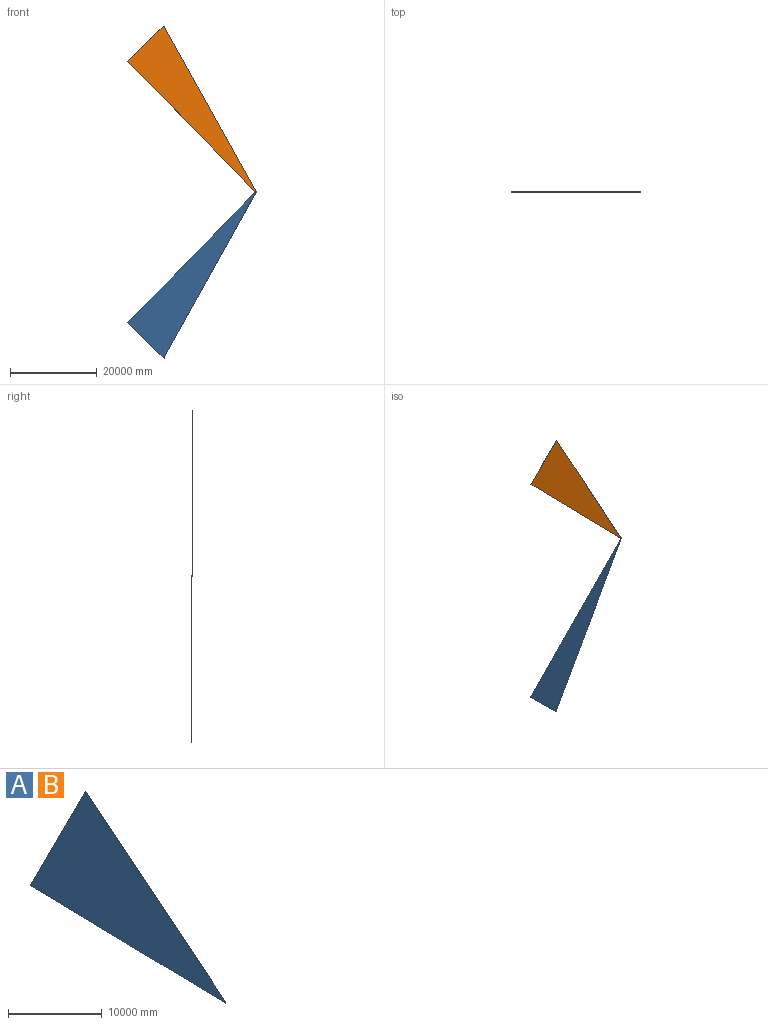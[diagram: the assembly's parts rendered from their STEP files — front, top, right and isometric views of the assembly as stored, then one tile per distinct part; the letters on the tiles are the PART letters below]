
ASSEMBLY  parts=2 mates=1
PART A: 16 faces, bbox 29537x197.9x38271.4 mm
  f0: plane 12.51x11.03mm, normal (0,-1,0), area 34.1mm2, adj f1,f7,f15
  f1: plane 87.66x10.3mm, normal (-0.97,0,-0.24), area 931.1mm2, adj f0,f2,f7,f8,f9,f13,f15
  f2: plane 87.66x8.75mm, normal (-0.75,0,0.67), area 1027.2mm2, adj f1,f3,f8,f9
  f3: plane 87.66x63.01mm, normal (-0.64,0,-0.77), area 7198.1mm2, adj f2,f4,f8,f9
  f4: plane 87.66x83.8mm, normal (0.7,0,-0.72), area 10239.7mm2, adj f3,f5,f8,f9,f11
  f5: plane 87.66x79.55mm, normal (0.87,0,0.49), area 7975.6mm2, adj f4,f6,f9,f10
  f6: plane 87.66x84.93mm, normal (-0.7,0,0.71), area 10412.2mm2, adj f5,f7,f9,f15
  f7: plane 87.66x12.51mm, normal (-0.44,0,0.9), area 1223mm2, adj f0,f1,f6,f9
  f8: plane 65.64x61.8mm, normal (0,-1,0), area 640.3mm2, adj f1,f2,f3,f4,f13
  f9: plane 160.94x146.81mm, normal (0,1,0), area 11632mm2, adj f1,f2,f3,f4,f5,f6,f7
  f10: plane 38190.04x21206.94mm, normal (0.87,0,0.49), area 1608841.7mm2, adj f5,f11,f12,f14,f15
  f11: plane 81.22x78.89mm, normal (0.7,0,-0.72), area 4150.4mm2, adj f4,f10,f13,f14
  f12: plane 8330.07x8145.44mm, normal (-0.7,0,0.71), area 429092.1mm2, adj f10,f13,f14,f15
  f13: plane 30123.49x29455.8mm, normal (-0.71,0,-0.7), area 1551698.8mm2, adj f1,f8,f11,f12,f14,f15
  f14: plane 38268.83x29536.93mm, normal (0,-1,0), area 247815295.6mm2, adj f10,f11,f12,f13
  f15: plane 38209.58x29492.76mm, normal (0,1,0), area 247804338mm2, adj f0,f1,f6,f10,f12,f13
PART B: same geometry as A
PLACE A rot(axis=(1,0,0),180deg) t=(16.2,-130.1,55.15)mm
PLACE B t=(16.2,45.21,-10.46)mm
MATE revolute A.f0 <-> B.f0  axis (0,1,0) through (-96.64,-42.44,22.35)mm
